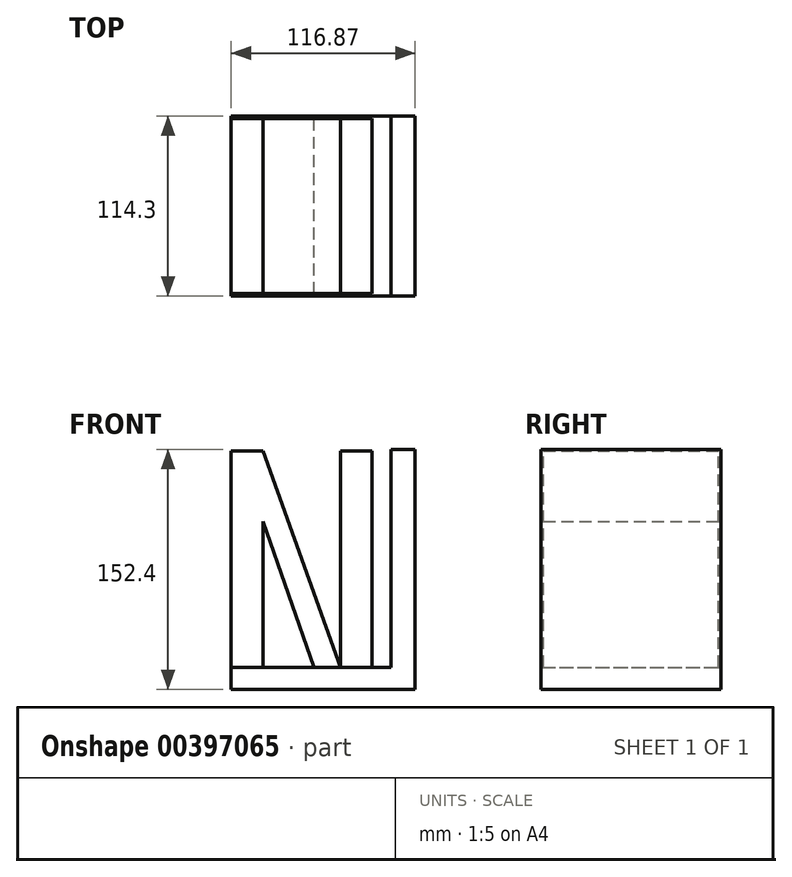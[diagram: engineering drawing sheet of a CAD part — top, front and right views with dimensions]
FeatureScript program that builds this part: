
annotation { "Feature Type Name" : "Feature", "Feature Type Description" : "" }
export const myFeature = defineFeature(function(context is Context, id is Id, definition is map)
    precondition{}
    {
        {
            var Q0;
            Q0=qCreatedBy(makeId("Right.planeOp"),FACE);
            var sketch = newSketch(context, id + "F0", { "sketchPlane" : qUnion([Q0])});
            skLineSegment(sketch, "E0.bottom", {"start": v(-57.15, -76.2) * mm, "end": v(57.15, -76.2) * mm});
            skLineSegment(sketch, "E0.top", {"start": v(-57.15, 76.2) * mm, "end": v(57.15, 76.2) * mm});
            skLineSegment(sketch, "E0.left", {"start": v(-57.15, -76.2) * mm, "end": v(-57.15, 76.2) * mm});
            skLineSegment(sketch, "E0.right", {"start": v(57.15, -76.2) * mm, "end": v(57.15, 76.2) * mm});
            skPoint(sketch, "E0.middle", {"position": v(0, 0) * mm});
            skSolve(sketch);
        }
        {
            var Q0;
            Q0 = qSketchRegion(id + "F0", true);
            extrude(context, id + "F1", {"entities" : qUnion([Q0]), "depth" : 15.24 * mm});
        }
        {
            var Q0;
            Q0=qCreatedBy(makeId("Front.planeOp"),FACE);
            var sketch = newSketch(context, id + "F2", { "sketchPlane" : qUnion([Q0])});
            skLineSegment(sketch, "E1.bottom", {"start": v(0, -76.2) * mm, "end": v(-101.6, -76.2) * mm});
            skLineSegment(sketch, "E1.top", {"start": v(0, -62.08) * mm, "end": v(-101.6, -62.08) * mm});
            skLineSegment(sketch, "E1.left", {"start": v(0, -76.2) * mm, "end": v(0, -62.08) * mm});
            skLineSegment(sketch, "E1.right", {"start": v(-101.6, -76.2) * mm, "end": v(-101.6, -62.08) * mm});
            skSolve(sketch);
        }
        {
            var Q0;
            Q0=makeQuery(id+"F2.imprint","IMPRINT",FACE,{"disambiguationData":[TD([[makeQuery(id+"F2.imprint","IMPRINT",EDGE,{"derivedFrom":sQuery(id+"F2.wireOp",EDGE,"E1.bottom")}),-1.0]])]});
            extrude(context, id + "F3", {"entities" : qUnion([Q0]), "operationType" : NewBodyOperationType.ADD, "depth" : 57.15 * mm});
        }
        {
            var Q0;
            Q0 = qSketchRegion(id + "F2", true);
            extrude(context, id + "F4", {"entities" : qUnion([Q0]), "operationType" : NewBodyOperationType.ADD, "oppositeDirection" : true, "depth" : 57.15 * mm});
        }
        {
            var Q0;
            Q0=qCreatedBy(makeId("Front.planeOp"),FACE);
            var sketch = newSketch(context, id + "F5", { "sketchPlane" : qUnion([Q0])});
            skLineSegment(sketch, "E2.bottom", {"start": v(-101.63, -62.08) * mm, "end": v(-81.49, -62.08) * mm});
            skLineSegment(sketch, "E2.top", {"start": v(-101.63, 75.2) * mm, "end": v(-81.49, 75.2) * mm});
            skLineSegment(sketch, "E2.left", {"start": v(-101.63, -62.08) * mm, "end": v(-101.63, 75.2) * mm});
            skLineSegment(sketch, "E2.right", {"start": v(-81.49, -62.08) * mm, "end": v(-81.49, 75.2) * mm});
            skLineSegment(sketch, "E3", {"start": v(-81.49, 75.2) * mm, "end": v(-32.27, -62.08) * mm});
            skLineSegment(sketch, "E4", {"start": v(-81.49, 30.6) * mm, "end": v(-48.96, -62.08) * mm});
            skLineSegment(sketch, "E5.bottom", {"start": v(-32.27, -62.08) * mm, "end": v(-12.12, -62.08) * mm});
            skLineSegment(sketch, "E5.top", {"start": v(-32.27, 75.2) * mm, "end": v(-12.12, 75.2) * mm});
            skLineSegment(sketch, "E5.left", {"start": v(-32.27, -62.08) * mm, "end": v(-32.27, 75.2) * mm});
            skLineSegment(sketch, "E5.right", {"start": v(-12.12, -62.08) * mm, "end": v(-12.12, 75.2) * mm});
            skLineSegment(sketch, "E6", {"start": v(-48.96, -62.08) * mm, "end": v(-32.27, -62.08) * mm});
            skSolve(sketch);
        }
        {
            var Q0;
            Q0 = qSketchRegion(id + "F5", true);
            extrude(context, id + "F6", {"entities" : qUnion([Q0]), "operationType" : NewBodyOperationType.ADD, "depth" : 55.63 * mm});
        }
        {
            var Q0;
            Q0 = qSketchRegion(id + "F5", true);
            extrude(context, id + "F7", {"entities" : qUnion([Q0]), "operationType" : NewBodyOperationType.ADD, "oppositeDirection" : true, "depth" : 55.63 * mm});
        }
    });
